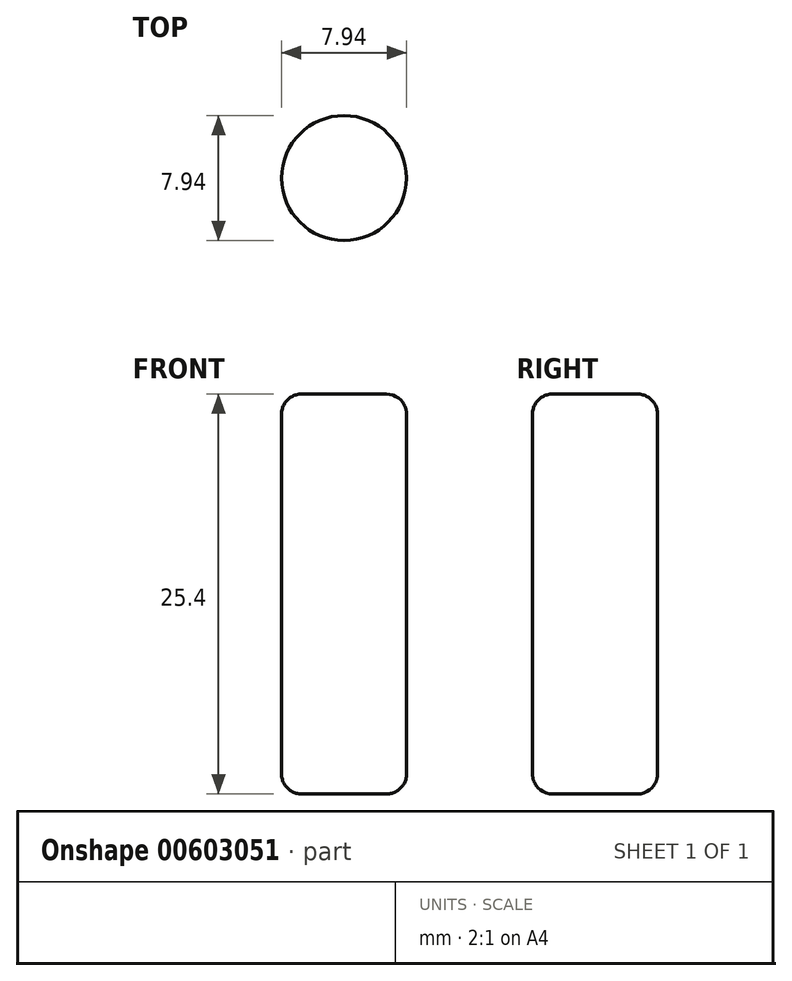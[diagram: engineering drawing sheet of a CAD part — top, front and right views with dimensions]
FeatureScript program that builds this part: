
annotation { "Feature Type Name" : "Feature", "Feature Type Description" : "" }
export const myFeature = defineFeature(function(context is Context, id is Id, definition is map)
    precondition{}
    {
        {
            var Q0;
            Q0=qCreatedBy(makeId("Front.planeOp"),FACE);
            var sketch = newSketch(context, id + "F0", { "sketchPlane" : qUnion([Q0])});
            skLineSegment(sketch, "E0", {"start": v(-19.43, 0) * mm, "end": v(-19.43, 25.4) * mm});
            skLineSegment(sketch, "E1", {"start": v(-19.43, 25.4) * mm, "end": v(-23.4, 25.4) * mm});
            skLineSegment(sketch, "E2", {"start": v(-23.4, 25.4) * mm, "end": v(-23.4, 0) * mm});
            skLineSegment(sketch, "E3", {"start": v(-23.4, 0) * mm, "end": v(-19.43, 0) * mm});
            skSolve(sketch);
        }
        {
            var Q0;
            Q0=makeQuery(id+"F0.imprint","IMPRINT",FACE,{"disambiguationData":[TD([[makeQuery(id+"F0.imprint","IMPRINT",EDGE,{"derivedFrom":sQuery(id+"F0.wireOp",EDGE,"E0")}),1.0]])]});
            var Q1;
            Q1=sQuery(id+"F0.wireOp",EDGE,"E0");
            revolve(context, id + "F1", {"entities" : qUnion([Q0]), "axis" : qUnion([Q1]), "revolveType" : RevolveType.FULL});
        }
        {
            var Q0;
            Q0=makeQuery(id+"F1.opRevolve","SWEPT_EDGE",EDGE,{"disambiguationData":[OSD([sQuery(id+"F0.wireOp",EDGE,"E1"),sQuery(id+"F0.wireOp",EDGE,"E2")])]});
            var Q1;
            Q1=makeQuery(id+"F1.opRevolve","SWEPT_EDGE",EDGE,{"disambiguationData":[OSD([sQuery(id+"F0.wireOp",EDGE,"E2"),sQuery(id+"F0.wireOp",EDGE,"E3")])]});
            fillet(context, id + "F2", {"entities" : qUnion([Q0, Q1]), "radius" : 1.27 * mm, "tangentPropagation" : true, "allowEdgeOverflow" : false});
        }
    });
